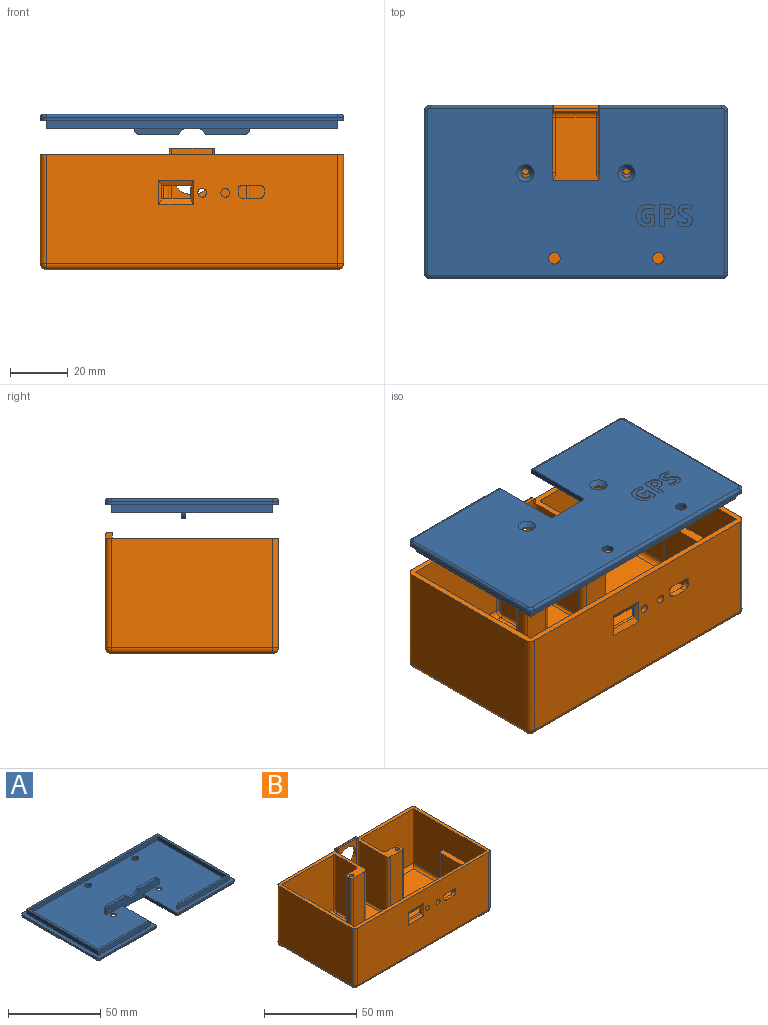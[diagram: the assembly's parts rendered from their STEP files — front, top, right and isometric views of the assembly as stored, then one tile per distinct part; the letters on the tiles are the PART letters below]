
ASSEMBLY  parts=2 mates=1
PART A: 121 faces, bbox 105.3x60.3x7 mm
  f0: plane 103x58mm, normal (0,0,-1), area 5410.3mm2, adj f6,f7,f22,f31,f32,f41,f42,f43
  f1: plane 40x5mm, normal (0,1,0), area 178.5mm2, adj f2,f9,f23,f24,f25,f28,f35,f36
  f2: plane 13.42x1.6mm, normal (0,0,1), area 21.5mm2, adj f1,f22,f28,f35
  f3: plane 38.5x3mm, normal (0,1,0), area 114.6mm2, adj f5,f9,f19,f27,f33
  f4: plane 39.8x3mm, normal (0,-1,0), area 118.5mm2, adj f5,f9,f17,f26,f34
  f5: plane 100.6x55.6mm, normal (0,0,1), area 366.9mm2, adj f3,f4,f10,f15,f16,f17,f18,f19
  f6: plane 25.2x2mm, normal (1,0,0), area 50.2mm2, adj f0,f9,f12,f49,f51
  f7: plane 25.2x2mm, normal (-1,0,0), area 50.2mm2, adj f0,f8,f9,f41,f50
  f8: plane 42.5x1mm, normal (0,-1,0), area 42.5mm2, adj f7,f9,f38,f41
  f9: plane 105x60mm, normal (0,0,1), area 5402.5mm2, adj f1,f3,f4,f6,f7,f8,f10,f11
  f10: plane 39.8x3mm, normal (0,-1,0), area 118.5mm2, adj f5,f9,f16,f27,f33
  f11: plane 56x1mm, normal (-1,0,0), area 56mm2, adj f9,f37,f40,f47
  f12: plane 42.5x1mm, normal (0,-1,0), area 42.5mm2, adj f6,f9,f37,f49
  f13: plane 56x1mm, normal (1,0,0), area 56mm2, adj f9,f38,f39,f43
  f14: plane 101x1mm, normal (0,1,0), area 101mm2, adj f9,f39,f40,f45
  f15: plane 100.6x3mm, normal (0,1,0), area 301.8mm2, adj f5,f9,f16,f17
  f16: plane 55.6x3mm, normal (-1,0,0), area 166.8mm2, adj f5,f9,f10,f15
  f17: plane 55.6x3mm, normal (1,0,0), area 166.8mm2, adj f4,f5,f9,f15
  f18: plane 98x3mm, normal (0,-1,0), area 294mm2, adj f5,f9,f19,f21
  f19: plane 53x3mm, normal (1,0,0), area 159mm2, adj f3,f5,f9,f18
  f20: plane 38.5x3mm, normal (0,1,0), area 114.6mm2, adj f5,f9,f21,f26,f34
  f21: plane 53x3mm, normal (-1,0,0), area 159mm2, adj f5,f9,f18,f20
  f22: plane 40x7mm, normal (0,-1,0), area 206.5mm2, adj f0,f2,f9,f23,f24,f25,f28,f35
  f23: plane 3x1.6mm, normal (1,0,0), area 4.8mm2, adj f1,f9,f22,f35
  f24: plane 3x1.6mm, normal (-1,0,0), area 4.8mm2, adj f1,f9,f22,f36
  f25: plane 13.42x1.6mm, normal (0,0,1), area 21.5mm2, adj f1,f22,f28,f36
  f26: plane 1.3x1mm, normal (-1,0,0), area 1.3mm2, adj f4,f9,f20,f34
  f27: plane 1.3x1mm, normal (1,0,0), area 1.3mm2, adj f3,f9,f10,f33
  f28: cylinder r=5mm len=9.17mm, axis (0,1,0), area 18.5mm2, adj f1,f2,f22,f25
  f29: cylinder r=1.5mm len=3mm, axis (0,0,1), area 4.7mm2, adj f9,f31
  f30: cylinder r=1.5mm len=3mm, axis (0,0,1), area 4.7mm2, adj f9,f32
  f31: cone r=3mm half-angle=45deg, axis (0,0,-1), area 30mm2, adj f0,f29
  f32: cone r=3mm half-angle=45deg, axis (0,0,-1), area 30mm2, adj f0,f30
  f33: cylinder r=2mm len=2mm, axis (0,1,0), area 4.1mm2, adj f3,f5,f10,f27
  f34: cylinder r=2mm len=2mm, axis (0,-1,0), area 4.1mm2, adj f4,f5,f20,f26
  f35: cylinder r=2mm len=2mm, axis (0,-1,0), area 5mm2, adj f1,f2,f22,f23
  f36: cylinder r=2mm len=2mm, axis (0,1,0), area 5mm2, adj f1,f22,f24,f25
  f37: cylinder r=2mm len=2mm, axis (0,0,1), area 3.1mm2, adj f9,f11,f12,f48
  f38: cylinder r=2mm len=2mm, axis (0,0,-1), area 3.1mm2, adj f8,f9,f13,f42
  f39: cylinder r=2mm len=2mm, axis (0,0,1), area 3.1mm2, adj f9,f13,f14,f44
  f40: cylinder r=2mm len=2mm, axis (0,0,-1), area 3.1mm2, adj f9,f11,f14,f46
  f41: cylinder r=1mm len=42.5mm, axis (1,0,0), area 66.8mm2, adj f0,f7,f8,f42
  f42: torus R=1mm, axis (0,0,1), area 4mm2, adj f0,f38,f41,f43
  f43: cylinder r=1mm len=56mm, axis (0,1,0), area 88mm2, adj f0,f13,f42,f44
  f44: torus R=1mm, axis (0,0,1), area 4mm2, adj f0,f39,f43,f45
  f45: cylinder r=1mm len=101mm, axis (-1,0,0), area 158.7mm2, adj f0,f14,f44,f46
  f46: torus R=1mm, axis (0,0,1), area 4mm2, adj f0,f40,f45,f47
  f47: cylinder r=1mm len=56mm, axis (0,-1,0), area 88mm2, adj f0,f11,f46,f48
  f48: torus R=1mm, axis (0,0,1), area 4mm2, adj f0,f37,f47,f49
  f49: cylinder r=1mm len=42.5mm, axis (1,0,0), area 66.8mm2, adj f0,f6,f12,f48
  f50: cylinder r=1mm len=2mm, axis (0,0,1), area 3.1mm2, adj f0,f7,f9,f22
  f51: cylinder r=1mm len=2mm, axis (0,0,-1), area 3.1mm2, adj f0,f6,f9,f22
  f52: cylinder r=2mm len=4mm, axis (0,0,-1), area 25.1mm2, adj f0,f9
  f53: cylinder r=2mm len=4mm, axis (0,0,-1), area 25.1mm2, adj f0,f9
  f54: extruded ~1.89x0.77mm, area 0.6mm2, adj f0,f55,f69,f70
  f55: extruded ~1.78x0.72mm, area 0.6mm2, adj f0,f54,f56,f70
  f56: extruded ~2.11x0.6mm, area 0.7mm2, adj f0,f55,f57,f70
  f57: plane 2.44x0.3mm, normal (0,1,0), area 0.7mm2, adj f0,f56,f58,f70
  f58: plane 7.64x0.3mm, normal (1,0,0), area 2.3mm2, adj f0,f57,f59,f70
  f59: plane 1.62x0.3mm, normal (0,-1,0), area 0.5mm2, adj f0,f58,f60,f70
  f60: plane 2.72x0.3mm, normal (-1,0,0), area 0.8mm2, adj f0,f59,f61,f70
  f61: plane 0.69x0.3mm, normal (0,-1,0), area 0.2mm2, adj f0,f60,f69,f70
  f62: plane 0.53x0.3mm, normal (0,1,0), area 0.2mm2, adj f63,f68,f70,f71
  f63: plane 2.27x0.3mm, normal (-1,0,0), area 0.7mm2, adj f62,f64,f70,f71
  f64: plane 0.74x0.3mm, normal (0,-1,0), area 0.2mm2, adj f63,f65,f70,f71
  f65: extruded ~0.97x0.3mm, area 0.3mm2, adj f64,f66,f70,f71
  f66: extruded ~0.84x0.31mm, area 0.3mm2, adj f65,f67,f70,f71
  f67: extruded ~0.86x0.37mm, area 0.3mm2, adj f66,f68,f70,f71
  f68: extruded ~1.12x0.3mm, area 0.4mm2, adj f62,f67,f70,f71
  f69: extruded ~2.19x0.65mm, area 0.7mm2, adj f0,f54,f61,f70
  f70: plane 7.64x5.28mm, normal (0,0,-1), area 23.8mm2, adj f54,f55,f56,f57,f58,f59,f60,f61
  f71: plane 2.27x2.02mm, normal (0,0,-1), area 4.1mm2, adj f62,f63,f64,f65,f66,f67,f68
  f72: extruded ~1.63x0.75mm, area 0.6mm2, adj f0,f73,f99,f100
  f73: extruded ~1.26x0.4mm, area 0.4mm2, adj f0,f72,f74,f100
  f74: extruded ~1.47x1.03mm, area 0.5mm2, adj f0,f73,f75,f100
  f75: extruded ~1.03x0.54mm, area 0.3mm2, adj f0,f74,f76,f100
  f76: extruded ~0.32x0.31mm, area 0.1mm2, adj f0,f75,f77,f100
  f77: extruded ~0.37x0.3mm, area 0.1mm2, adj f0,f76,f78,f100
  f78: extruded ~0.56x0.3mm, area 0.2mm2, adj f0,f77,f79,f100
  f79: extruded ~0.71x0.3mm, area 0.2mm2, adj f0,f78,f80,f100
  f80: extruded ~0.79x0.3mm, area 0.2mm2, adj f0,f79,f81,f100
  f81: extruded ~1.01x0.35mm, area 0.3mm2, adj f0,f80,f82,f100
  f82: plane 1.26x0.52mm, normal (-0.92,-0.38,0), area 0.4mm2, adj f0,f81,f83,f100
  f83: extruded ~1.13x0.4mm, area 0.4mm2, adj f0,f82,f84,f100
  f84: extruded ~1.14x0.3mm, area 0.3mm2, adj f0,f83,f85,f100
  f85: extruded ~1.9x0.58mm, area 0.6mm2, adj f0,f84,f86,f100
  f86: extruded ~1.59x0.69mm, area 0.5mm2, adj f0,f85,f87,f100
  f87: extruded ~0.94x0.3mm, area 0.3mm2, adj f0,f86,f88,f100
  f88: extruded ~0.71x0.56mm, area 0.3mm2, adj f0,f87,f89,f100
  f89: extruded ~1.05x0.63mm, area 0.4mm2, adj f0,f88,f90,f100
  f90: extruded ~0.99x0.52mm, area 0.3mm2, adj f0,f89,f91,f100
  f91: extruded ~0.37x0.34mm, area 0.2mm2, adj f0,f90,f92,f100
  f92: extruded ~0.4x0.3mm, area 0.1mm2, adj f0,f91,f93,f100
  f93: extruded ~0.61x0.3mm, area 0.2mm2, adj f0,f92,f94,f100
  f94: extruded ~0.82x0.3mm, area 0.3mm2, adj f0,f93,f95,f100
  f95: extruded ~0.98x0.3mm, area 0.3mm2, adj f0,f94,f96,f100
  f96: extruded ~1.31x0.49mm, area 0.4mm2, adj f0,f95,f97,f100
  f97: plane 1.5x0.3mm, normal (1,0,0), area 0.5mm2, adj f0,f96,f98,f100
  f98: extruded ~2.16x0.46mm, area 0.7mm2, adj f0,f97,f99,f100
  f99: extruded ~2.07x0.6mm, area 0.7mm2, adj f0,f72,f98,f100
  f100: plane 7.85x4.98mm, normal (0,0,-1), area 22mm2, adj f72,f73,f74,f75,f76,f77,f78,f79
  f101: plane 3.03x0.3mm, normal (0,1,0), area 0.9mm2, adj f0,f102,f119,f120
  f102: plane 1.35x0.3mm, normal (1,0,0), area 0.4mm2, adj f0,f101,f103,f120
  f103: plane 1.45x0.3mm, normal (0,-1,0), area 0.4mm2, adj f0,f102,f104,f120
  f104: plane 1.59x0.3mm, normal (1,0,0), area 0.5mm2, adj f0,f103,f105,f120
  f105: extruded ~1.03x0.3mm, area 0.3mm2, adj f0,f104,f106,f120
  f106: extruded ~1.48x0.66mm, area 0.5mm2, adj f0,f105,f107,f120
  f107: extruded ~1.9x0.51mm, area 0.6mm2, adj f0,f106,f108,f120
  f108: extruded ~1.9x0.63mm, area 0.6mm2, adj f0,f107,f109,f120
  f109: extruded ~1.68x0.71mm, area 0.6mm2, adj f0,f108,f110,f120
  f110: extruded ~1.74x0.42mm, area 0.5mm2, adj f0,f109,f111,f120
  f111: plane 1.3x0.54mm, normal (-0.92,-0.38,0), area 0.4mm2, adj f0,f110,f112,f120
  f112: extruded ~2.27x0.47mm, area 0.7mm2, adj f0,f111,f113,f120
  f113: extruded ~2.93x1.03mm, area 1mm2, adj f0,f112,f114,f120
  f114: extruded ~2.88x1.06mm, area 0.9mm2, adj f0,f113,f115,f120
  f115: extruded ~2.92x0.91mm, area 0.9mm2, adj f0,f114,f116,f120
  f116: extruded ~2.64x1.02mm, area 0.9mm2, adj f0,f115,f117,f120
  f117: extruded ~1.33x0.3mm, area 0.4mm2, adj f0,f116,f118,f120
  f118: extruded ~1.39x0.34mm, area 0.4mm2, adj f0,f117,f119,f120
  f119: plane 3.96x0.3mm, normal (-1,0,0), area 1.2mm2, adj f0,f101,f118,f120
  f120: plane 7.85x6.27mm, normal (0,0,-1), area 28.4mm2, adj f101,f102,f103,f104,f105,f106,f107,f108
PART B: 118 faces, bbox 105x60x42 mm
  f0: plane 101x36mm, normal (0,1,0), area 3400.5mm2, adj f2,f3,f14,f16,f17,f19,f20,f37
  f1: plane 101x38mm, normal (0,-1,0), area 3683.5mm2, adj f3,f49,f50,f51,f52,f53,f54,f55
  f2: plane 56x36mm, normal (1,0,0), area 1352mm2, adj f0,f3,f13,f18,f20,f40,f42,f44
  f3: plane 105x60mm, normal (0,0,1), area 792.4mm2, adj f0,f1,f2,f4,f6,f7,f8,f9
  f4: plane 37x15.25mm, normal (-1,0,0), area 564mm2, adj f3,f59,f96,f97,f98
  f5: plane 97x52mm, normal (0,0,1), area 4671.3mm2, adj f16,f19,f63,f64,f65,f66,f67,f68
  f6: plane 37x15.25mm, normal (1,0,0), area 564mm2, adj f3,f60,f93,f94,f95
  f7: plane 37x9mm, normal (0,-1,0), area 333mm2, adj f3,f62,f85,f86
  f8: plane 39.5x36mm, normal (0,-1,0), area 1422mm2, adj f3,f14,f65,f95
  f9: plane 101x39mm, normal (0,1,0), area 3710.5mm2, adj f3,f25,f34,f35,f74,f78,f80,f113
  f10: plane 56x38mm, normal (-1,0,0), area 2128mm2, adj f3,f71,f77,f80
  f11: plane 56x38mm, normal (1,0,0), area 2128mm2, adj f3,f69,f73,f74
  f12: plane 101x56mm, normal (0,0,-1), area 5656mm2, adj f72,f73,f77,f78
  f13: plane 39.5x36mm, normal (0,-1,0), area 1422mm2, adj f2,f3,f67,f96
  f14: plane 56x36mm, normal (-1,0,0), area 1352mm2, adj f0,f3,f8,f15,f17,f38,f39,f43
  f15: plane 22x2mm, normal (0,1,0), area 43.1mm2, adj f14,f17,f64,f115
  f16: plane 32x22mm, normal (-1,0,0), area 703.1mm2, adj f0,f5,f17,f66,f115
  f17: plane 33x3mm, normal (0,0,1), area 98.8mm2, adj f0,f14,f15,f16,f115
  f18: plane 22x2mm, normal (0,1,0), area 43.1mm2, adj f2,f20,f68,f114
  f19: plane 32x22mm, normal (1,0,0), area 703.1mm2, adj f0,f5,f20,f66,f114
  f20: plane 33x3mm, normal (0,0,1), area 98.8mm2, adj f0,f2,f18,f19,f114
  f21: plane 37x9mm, normal (0,-1,0), area 333mm2, adj f3,f61,f104,f106
  f22: plane 37x20.25mm, normal (1,0,0), area 749mm2, adj f3,f61,f108,f109,f110
  f23: plane 37x20.25mm, normal (-1,0,0), area 749mm2, adj f3,f62,f81,f82,f83
  f24: plane 38x14mm, normal (0,-1,0), area 388.9mm2, adj f25,f36,f63,f81,f110
  f25: cylinder r=6.75mm len=13.5mm, axis (0,1,0), area 84.8mm2, adj f9,f24
  f26: plane 37x3mm, normal (1,0,0), area 111mm2, adj f3,f86,f88,f89
  f27: plane 37x7mm, normal (0,1,0), area 259mm2, adj f3,f60,f89,f91
  f28: plane 37x7mm, normal (0,1,0), area 259mm2, adj f3,f59,f100,f101
  f29: plane 37x3mm, normal (-1,0,0), area 111mm2, adj f3,f101,f103,f104
  f30: cylinder r=1.25mm len=35mm, axis (0,0,1), area 274.9mm2, adj f3,f31
  f31: plane 2.5x2.5mm, normal (0,0,1), area 4.9mm2, adj f30
  f32: cylinder r=1.25mm len=35mm, axis (0,0,1), area 274.9mm2, adj f3,f33
  f33: plane 2.5x2.5mm, normal (0,0,1), area 4.9mm2, adj f32
  f34: plane 2.4x2mm, normal (-1,0,0), area 4.6mm2, adj f3,f9,f36,f110,f113
  f35: plane 2.4x2mm, normal (1,0,0), area 4.6mm2, adj f3,f9,f36,f81,f113
  f36: plane 15.6x1.4mm, normal (0,0,1), area 15.8mm2, adj f24,f34,f35,f81,f110,f113
  f37: plane 3x2mm, normal (-1,0,0), area 4mm2, adj f0,f38,f39,f43
  f38: plane 3x2mm, normal (0,0,1), area 6mm2, adj f0,f14,f37,f39
  f39: plane 3x1mm, normal (0,1,0), area 3mm2, adj f14,f37,f38,f43
  f40: plane 3x2mm, normal (0,0,1), area 6mm2, adj f0,f2,f41,f42
  f41: plane 3x2mm, normal (1,0,0), area 4mm2, adj f0,f40,f42,f44
  f42: plane 3x1mm, normal (0,1,0), area 3mm2, adj f2,f40,f41,f44
  f43: plane 3x2mm, normal (0,0.71,-0.71), area 8.5mm2, adj f0,f14,f37,f39
  f44: plane 3x2mm, normal (0,0.71,-0.71), area 8.5mm2, adj f0,f2,f41,f42
  f45: plane 10x1mm, normal (0,0,1), area 10mm2, adj f0,f46,f48,f117
  f46: plane 4.5x1mm, normal (-1,0,0), area 4.5mm2, adj f0,f45,f47,f56
  f47: plane 10x1mm, normal (0,0,-1), area 10mm2, adj f0,f46,f48,f116
  f48: plane 4.5x1mm, normal (1,0,0), area 4.5mm2, adj f0,f45,f47,f55
  f49: plane 7x2mm, normal (0,0,-1), area 14mm2, adj f0,f1,f111,f112
  f50: plane 2x1.5mm, normal (1,0,0), area 3mm2, adj f0,f1,f58,f112
  f51: plane 5x2mm, normal (0,0,1), area 10mm2, adj f0,f1,f57,f58
  f52: plane 2x1.5mm, normal (-1,0,0), area 3mm2, adj f0,f1,f57,f111
  f53: cylinder r=1.5mm len=3mm, axis (0,-1,0), area 18.8mm2, adj f0,f1
  f54: cylinder r=1.5mm len=3mm, axis (0,-1,0), area 18.8mm2, adj f0,f1
  f55: plane 8.5x1mm, normal (0.71,-0.71,0), area 9.2mm2, adj f1,f48,f116,f117
  f56: plane 8.5x1mm, normal (-0.71,-0.71,0), area 9.2mm2, adj f1,f46,f116,f117
  f57: cylinder r=2mm len=2mm, axis (0,-1,0), area 6.3mm2, adj f0,f1,f51,f52
  f58: cylinder r=2mm len=2mm, axis (0,1,0), area 6.3mm2, adj f0,f1,f50,f51
  f59: cylinder r=2mm len=37mm, axis (0,0,1), area 116.2mm2, adj f3,f4,f28,f99
  f60: cylinder r=2mm len=37mm, axis (0,0,1), area 116.2mm2, adj f3,f6,f27,f92
  f61: cylinder r=2mm len=37mm, axis (0,0,-1), area 116.2mm2, adj f3,f21,f22,f107
  f62: cylinder r=2mm len=37mm, axis (0,0,1), area 116.2mm2, adj f3,f7,f23,f84
  f63: cylinder r=2mm len=14mm, axis (-1,0,0), area 44mm2, adj f5,f24,f82,f109
  f64: cylinder r=2mm len=23mm, axis (0,1,0), area 70mm2, adj f5,f14,f15,f65
  f65: cylinder r=2mm len=39.5mm, axis (-1,0,0), area 121.8mm2, adj f5,f8,f64,f94
  f66: cylinder r=2mm len=95mm, axis (1,0,0), area 298.5mm2, adj f0,f5,f16,f19
  f67: cylinder r=2mm len=39.5mm, axis (-1,0,0), area 121.8mm2, adj f5,f13,f68,f97
  f68: cylinder r=2mm len=23mm, axis (0,-1,0), area 70mm2, adj f2,f5,f18,f67
  f69: cylinder r=2mm len=38mm, axis (0,0,1), area 119.4mm2, adj f1,f3,f11,f70
  f70: sphere r=2mm, area 6.3mm2, adj f69,f72,f73
  f71: cylinder r=2mm len=38mm, axis (0,0,-1), area 119.4mm2, adj f1,f3,f10,f75
  f72: cylinder r=2mm len=101mm, axis (1,0,0), area 317.3mm2, adj f1,f12,f70,f75
  f73: cylinder r=2mm len=56mm, axis (0,1,0), area 175.9mm2, adj f11,f12,f70,f76
  f74: cylinder r=2mm len=38mm, axis (0,0,-1), area 119.4mm2, adj f3,f9,f11,f76
  f75: sphere r=2mm, area 6.3mm2, adj f71,f72,f77
  f76: sphere r=2mm, area 6.3mm2, adj f73,f74,f78
  f77: cylinder r=2mm len=56mm, axis (0,-1,0), area 175.9mm2, adj f10,f12,f75,f79
  f78: cylinder r=2mm len=101mm, axis (-1,0,0), area 317.3mm2, adj f9,f12,f76,f79
  f79: sphere r=2mm, area 6.3mm2, adj f77,f78,f80
  f80: cylinder r=2mm len=38mm, axis (0,0,1), area 119.4mm2, adj f3,f9,f10,f79
  f81: cylinder r=1mm len=38mm, axis (0,0,1), area 58.4mm2, adj f3,f23,f24,f35,f36,f82
  f82: torus R=1mm, axis (1,0,0), area 4mm2, adj f23,f63,f81,f83
  f83: cylinder r=1mm len=19.25mm, axis (0,1,0), area 30.2mm2, adj f5,f23,f82,f84
  f84: torus R=3mm, axis (0,0,1), area 5.8mm2, adj f5,f62,f83,f85
  f85: cylinder r=1mm len=9mm, axis (1,0,0), area 14.1mm2, adj f5,f7,f84,f87
  f86: cylinder r=1mm len=37mm, axis (0,0,-1), area 58.1mm2, adj f3,f7,f26,f87
  f87: torus R=2mm, axis (0,0,1), area 3.4mm2, adj f5,f85,f86,f88
  f88: cylinder r=1mm len=3mm, axis (0,1,0), area 4.7mm2, adj f5,f26,f87,f90
  f89: cylinder r=1mm len=37mm, axis (0,0,1), area 58.1mm2, adj f3,f26,f27,f90
  f90: torus R=2mm, axis (0,0,1), area 3.4mm2, adj f5,f88,f89,f91
  f91: cylinder r=1mm len=7mm, axis (-1,0,0), area 11mm2, adj f5,f27,f90,f92
  f92: torus R=1mm, axis (0,0,1), area 4mm2, adj f5,f60,f91,f93
  f93: cylinder r=1mm len=14.25mm, axis (0,1,0), area 22.4mm2, adj f5,f6,f92,f94
  f94: torus R=1mm, axis (1,0,0), area 4mm2, adj f6,f65,f93,f95
  f95: cylinder r=1mm len=36mm, axis (0,0,1), area 56.5mm2, adj f3,f6,f8,f94
  f96: cylinder r=1mm len=36mm, axis (0,0,-1), area 56.5mm2, adj f3,f4,f13,f97
  f97: torus R=1mm, axis (1,0,0), area 4mm2, adj f4,f67,f96,f98
  f98: cylinder r=1mm len=14.25mm, axis (0,-1,0), area 22.4mm2, adj f4,f5,f97,f99
  f99: torus R=1mm, axis (0,0,1), area 4mm2, adj f5,f59,f98,f100
  f100: cylinder r=1mm len=7mm, axis (-1,0,0), area 11mm2, adj f5,f28,f99,f102
  f101: cylinder r=1mm len=37mm, axis (0,0,1), area 58.1mm2, adj f3,f28,f29,f102
  f102: torus R=2mm, axis (0,0,1), area 3.4mm2, adj f5,f100,f101,f103
  f103: cylinder r=1mm len=3mm, axis (0,-1,0), area 4.7mm2, adj f5,f29,f102,f105
  f104: cylinder r=1mm len=37mm, axis (0,0,1), area 58.1mm2, adj f3,f21,f29,f105
  f105: torus R=2mm, axis (0,0,1), area 3.4mm2, adj f5,f103,f104,f106
  f106: cylinder r=1mm len=9mm, axis (1,0,0), area 14.1mm2, adj f5,f21,f105,f107
  f107: torus R=3mm, axis (0,0,1), area 5.8mm2, adj f5,f61,f106,f108
  f108: cylinder r=1mm len=19.25mm, axis (0,-1,0), area 30.2mm2, adj f5,f22,f107,f109
  f109: torus R=1mm, axis (1,0,0), area 4mm2, adj f22,f63,f108,f110
  f110: cylinder r=1mm len=38mm, axis (0,0,-1), area 58.4mm2, adj f3,f22,f24,f34,f36,f109
  f111: cylinder r=1mm len=2mm, axis (0,1,0), area 3.1mm2, adj f0,f1,f49,f52
  f112: cylinder r=1mm len=2mm, axis (0,-1,0), area 3.1mm2, adj f0,f1,f49,f50
  f113: cylinder r=1mm len=15.6mm, axis (1,0,0), area 24.5mm2, adj f9,f34,f35,f36
  f114: cylinder r=1mm len=22mm, axis (0,0,1), area 34.6mm2, adj f5,f18,f19,f20
  f115: cylinder r=1mm len=22mm, axis (0,0,1), area 34.6mm2, adj f5,f15,f16,f17
  f116: plane 12x2mm, normal (0,-0.89,-0.45), area 24.6mm2, adj f1,f47,f55,f56
  f117: plane 12x2mm, normal (0,-0.89,0.45), area 24.6mm2, adj f1,f45,f55,f56
PLACE A rot(axis=(1,0,0),180deg) t=(-5.35,138.4,17.38)mm
PLACE B rot(axis=(-0.83,-0.49,0.25),0deg) t=(-5.26,149.13,-36.41)mm fixed
MATE slider B.f3 <-> A.f9  axis (0,0,1) through (-52.81,76.72,3.59)mm
